# Revit family: Haworth_Typical_Parametric_Compose_L_1Pack
name_source: partatom
category: Furniture Systems
units: mm (PartAtom-declared; Revit-internal decimal feet)

## family parameters
Always vertical = Yes
Cut with Voids When Loaded = No
OmniClass Number = 23.40.70.14.64.21
OmniClass Title = Systems Furniture
Part Type = Normal
Room Calculation Point = No
Round Connector Dimension = Use Diameter
Shared = No
Work Plane-Based = No

## types (1)
- 96w 72d - 42h Glass Stack, Lat, BF, Chair, Enlosure Panels, No Multi Panel Tiles
    Actual Off Spine Height = 42"
    Actual Off Spine Length = 72"
    Actual Off Spine Length Half = 36"
    Actual Off Spine Worksurface Depth = 30"
    Actual Spine Height = 42"
    Actual Spine Length = 96"
    Actual Spine Length Half = 48"
    Actual Spine Worksurface Depth = 24"
    Assembly Code = E2020200
    Box File = Yes
    Classic Pull = No
    Corner Length = 24"
    Crescent Pull = No
    Cushion Finish = Haworth _ Fabric _ Undecided _ Seating _ Lounge
    Description = Haworth_Typical_Parametric_Compose_L_1Pack
    Enclosure Panels = Yes
    File Cabinet Finish = Haworth _ Paint _ Undecided _ Pedestal
    File Depth = 29"
    File Drawer Finish = Haworth _ Paint _ Undecided _ Pedestal
    File Offset = 1/2"
    File Pull Finish = Haworth _ Paint _ Undecided _ Pedestal
    Glass Finish = Haworth _ Glass _ Undecided
    Glass Stack On Main Panels = Yes
    Hardware Finish = Haworth _ Paint _ Undecided _ Panel
    J Pull = Yes
    Lateral File = Yes
    Linear Pull = No
    Manufacturer = Haworth
    Max Height = 74"
    Max Length = 96"
    Max Length Wing = 60"
    Max Worksurface Depth = 30"
    Maximum Length = 96 in.
    Min Height = 34"
    Min Length = 60"
    Min Worksurface Depth = 18"
    Minimum Length = 60 in.
    Model = Haworth_Typical_Parametric_Compose_L_1Pack
    Multiple Panel Tiles = No
    Off Spine Height = 42"
    Off Spine Length = 72"
    Off Spine Straight Surface Length = 48"
    Off Spine Tile Count = 1
    Off Spine Worksurface Depth = 30"
    Panel High Tile Finish = Haworth _ Fabric _ Undecided _ Panel
    Panel Low Tile Finish = Haworth _ Fabric _ Undecided _ Panel
    Panel Thickness Half = 1 1/2"
    Radius Pull = No
    Revision = 1
    Seat Arm Cap Finish = Haworth _ Polymer _ Undecided
    Seat Back Upholstery Finish = Haworth _ Fabric _ Undecided _ Seating _ Task Back
    Seat Cushion Finish = Haworth _ Fabric _ Undecided _ Seating _ Task Seat
    Seat Shell Finish = Haworth _ Paint _ Undecided _ Seating
    Seat Support Finish = Haworth _ Polymer _ Undecided
    Single Panel Tile = Yes
    Size = Verify Final Dim. w/ Haworth
    Spine End Cap = No
    Spine End Panel Length = 72"
    Spine Height = 42"
    Spine Length = 96"
    Spine Tile Count = 1
    Spine Worksurface Depth = 24"
    Standard Panel Heights = 34, 42, 50, 58, 66, 74 in.
    Task Chair = Yes
    Tray Finish = Haworth _ Paint _ Undecided _ Panel
    URL = http://haworth.com
    URL - Product = http://haworth.com
    Wardrobe Height = 40 1/2"
    Worksurface Edge Finish = Haworth _ Laminate _ Undecided _ Tables
    Worksurface Finish = Haworth _ Laminate _ Undecided _ Tables

## geometry (parser evidence)
native form markers: Sweep x62
no freeform markers — native parametric forms only
